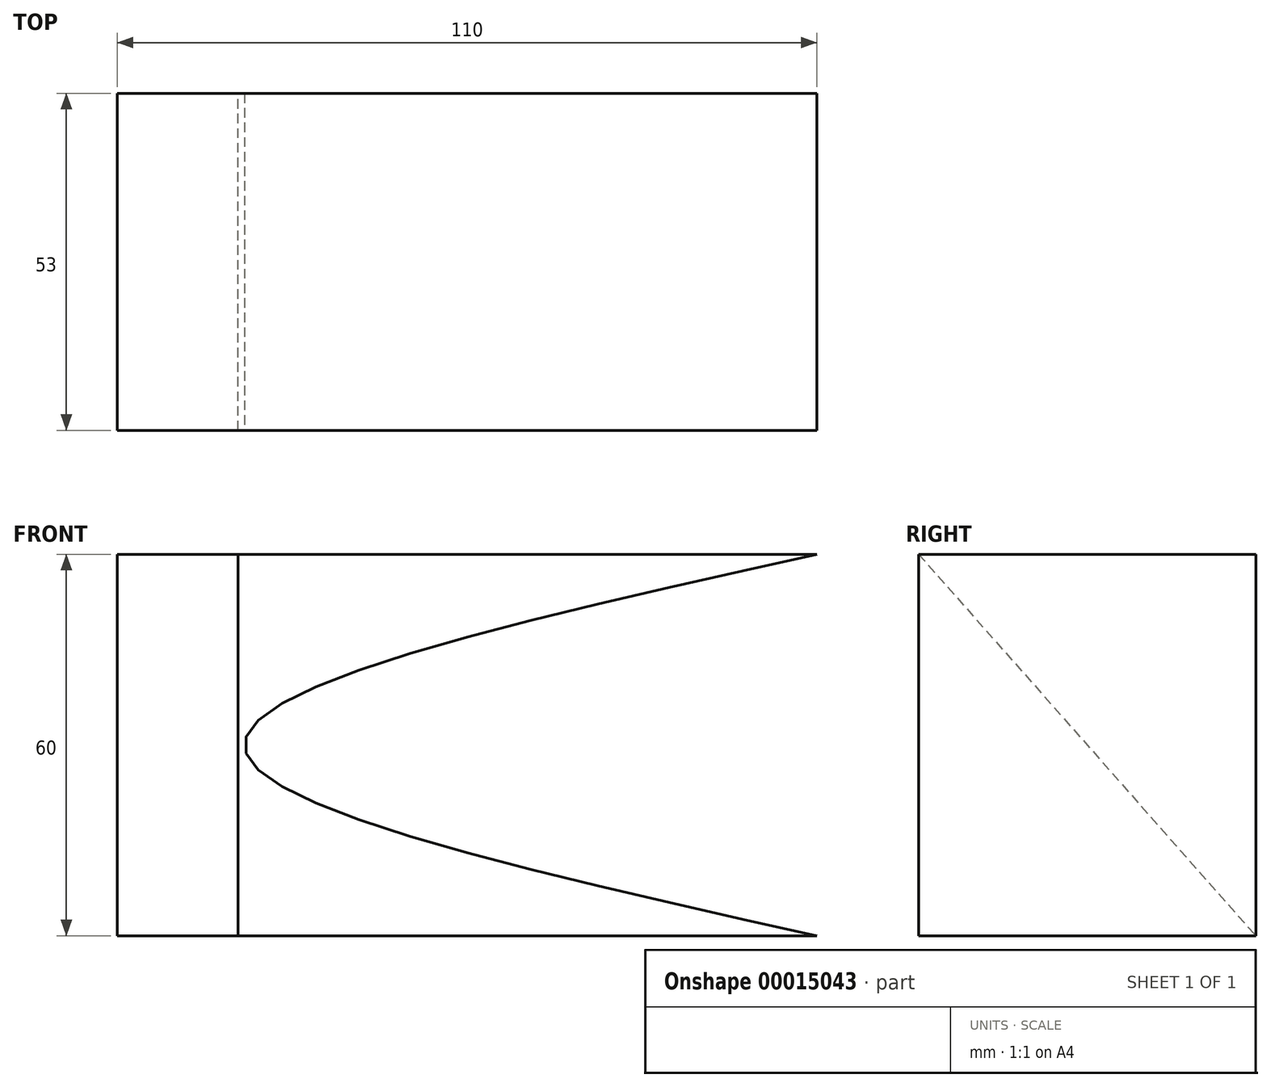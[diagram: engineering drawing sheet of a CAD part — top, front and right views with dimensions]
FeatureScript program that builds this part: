
annotation { "Feature Type Name" : "Feature", "Feature Type Description" : "" }
export const myFeature = defineFeature(function(context is Context, id is Id, definition is map)
    precondition{}
    {
        {
            var Q0;
            Q0=qCreatedBy(makeId("Front.planeOp"),FACE);
            var sketch = newSketch(context, id + "F0", { "sketchPlane" : qUnion([Q0])});
            skLineSegment(sketch, "E0.bottom", {"start": v(0, 0) * mm, "end": v(-110, 0) * mm});
            skLineSegment(sketch, "E0.top", {"start": v(0, 60) * mm, "end": v(-110, 60) * mm});
            skLineSegment(sketch, "E0.left", {"start": v(0, 0) * mm, "end": v(0, 60) * mm});
            skLineSegment(sketch, "E0.right", {"start": v(-110, 0) * mm, "end": v(-110, 60) * mm});
            skFitSpline(sketch, "E1", {"points": [v(0, 60) * mm, v(-90, 30) * mm, v(0, 0) * mm], "startDerivative": vector(-270, -60) * mm, "endDerivative": vector(270, -60) * mm});
            skSolve(sketch);
        }
        {
            var Q0;
            Q0=makeQuery(id+"F0.imprint","IMPRINT",FACE,{"disambiguationData":[TD([[makeQuery(id+"F0.imprint","IMPRINT",EDGE,{"derivedFrom":sQuery(id+"F0.wireOp",EDGE,"E0.bottom")}),-1.0]])]});
            extrude(context, id + "F1", {"entities" : qUnion([Q0]), "depth" : 53 * mm});
        }
        {
            var Q0;
            Q0=makeQuery(id+"F1.opExtrude","SWEPT_FACE",FACE,{"disambiguationData":[OSD([sQuery(id+"F0.wireOp",EDGE,"E0.right")])]});
            var sketch = newSketch(context, id + "F2", { "sketchPlane" : qUnion([Q0])});
            skLineSegment(sketch, "E2", {"start": v(0, 60) * mm, "end": v(53, 0) * mm});
            skLineSegment(sketch, "E3", {"start": v(53, 60) * mm, "end": v(0, 0) * mm});
            skCircle(sketch, "E4", {"center": v(26.5, 30) * mm, "radius": 3.75 * mm});
            skSolve(sketch);
        }
        {
            var Q0;
            {var subQ0=sQuery(id+"F2.wireOp",EDGE,"E4");var subQ3=sQuery(id+"F2.wireOp",EDGE,"E2");var subQ4=makeQuery(id+"F2.imprint","INTERSECT",VERTEX,{"disambiguationData":[OD(0.0)],"derivedFrom":[subQ3,subQ0]});Q0=makeQuery(id+"F2.imprint","IMPRINT",FACE,{"disambiguationData":[TD([[makeQuery(id+"F2.imprint","IMPRINT",EDGE,{"disambiguationData":[TD([[subQ4,-1.0]])],"derivedFrom":subQ3}),1.0]])]});}
            var Q1;
            {var subQ0=sQuery(id+"F2.wireOp",EDGE,"E4");var subQ3=sQuery(id+"F2.wireOp",EDGE,"E2");var subQ4=makeQuery(id+"F2.imprint","INTERSECT",VERTEX,{"disambiguationData":[OD(0.0)],"derivedFrom":[subQ3,subQ0]});Q1=makeQuery(id+"F2.imprint","IMPRINT",FACE,{"disambiguationData":[TD([[makeQuery(id+"F2.imprint","IMPRINT",EDGE,{"disambiguationData":[TD([[subQ4,-1.0]])],"derivedFrom":subQ3}),-1.0]])]});}
            var Q2;
            {var subQ1=sQuery(id+"F2.wireOp",EDGE,"E3");var subQ3=sQuery(id+"F2.wireOp",EDGE,"E2");var subQ5=makeQuery(id+"F2.imprint","INTERSECT",VERTEX,{"derivedFrom":[subQ3,subQ1]});Q2=makeQuery(id+"F2.imprint","IMPRINT",FACE,{"disambiguationData":[TD([[makeQuery(id+"F2.imprint","IMPRINT",EDGE,{"disambiguationData":[TD([[subQ5,-1.0]])],"derivedFrom":subQ3}),-1.0]])]});}
            var Q3;
            {var subQ1=sQuery(id+"F2.wireOp",EDGE,"E3");var subQ3=sQuery(id+"F2.wireOp",EDGE,"E2");var subQ5=makeQuery(id+"F2.imprint","INTERSECT",VERTEX,{"derivedFrom":[subQ3,subQ1]});Q3=makeQuery(id+"F2.imprint","IMPRINT",FACE,{"disambiguationData":[TD([[makeQuery(id+"F2.imprint","IMPRINT",EDGE,{"disambiguationData":[TD([[subQ5,-1.0]])],"derivedFrom":subQ3}),1.0]])]});}
            extrude(context, id + "F3", {"entities" : qUnion([Q0, Q1, Q2, Q3]), "operationType" : NewBodyOperationType.REMOVE, "oppositeDirection" : true, "depth" : 19 * mm});
        }
    });
